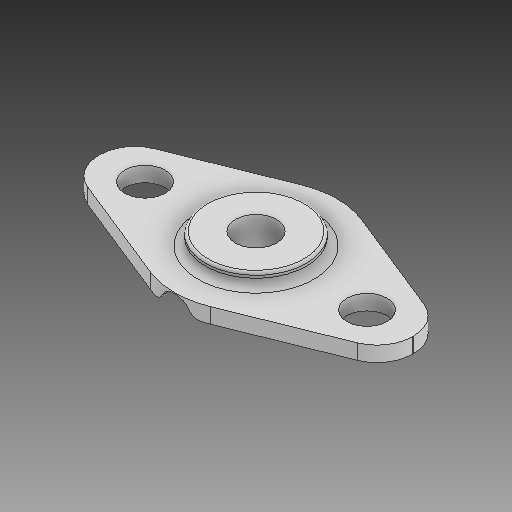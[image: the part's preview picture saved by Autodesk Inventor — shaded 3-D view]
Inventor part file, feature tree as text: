
AUTODESK INVENTOR PART (.ipt)
format: ipt  version: 2020 (Build 240168000, 168)  size: 327,168 bytes
history: native  units: mm
features: other x7, sketch x4, extrude x3, revolve x2, fillet x2, imported_body x1
ambient origin geometry x8: Origin, YZ Plane, XZ Plane, XY Plane, X Axis, Y Axis, Z Axis, Center Point
bodies: Solid1 (feature_tree)
feature tree (19):
  other  "HD_mastersketch.ipt"
  other  "Blocks"
  revolve  "Revolution1"  [1 undecoded]
  extrude  "Extrusion1"  Depth=5.0mm
  extrude  "Extrusion2"  TaperAngle=0.0deg  [1 undecoded]
  fillet  "Fillet1"  [1 undecoded]
  extrude  "Extrusion3"  Depth=3.6mm
  revolve  "Revolution2"  [1 undecoded]
  fillet  "Fillet3"  Radius=5.7mm
  other  "608 bearing"
  other  "Belt"
  other  "Rotor"
  imported_body  "Base"
  sketch  "Sketch8"  dims[d1=10.0mm d24=7.0mm d25=22.0mm d26=8.0mm]
  sketch  "Sketch9"  dims[d2=90.0deg d3=5.0mm d4=10.0mm]
  sketch  "Sketch10"  dims[d5=15.0mm d6=0.0mm d7=0.0mm d8=0.0mm d9=0.0mm]
  sketch  "Sketch14"  dims[d10=7.0mm d11=3.6mm d12=2.3mm d13=5.7mm d14=5.7mm d15=0.0mm d29=1.65mm d30=3.0mm d32=10.0mm d33=1.5mm d34=90.0deg d36=4.0mm d37=2.0mm]
  other  "608 bearing:1"
  other  "608 bearing:2"
note: 4 required parameter values undecoded (feature->parameter linkage not recoverable at this tier; creation-order binding heuristic only, values carry confidence <= 0.55)